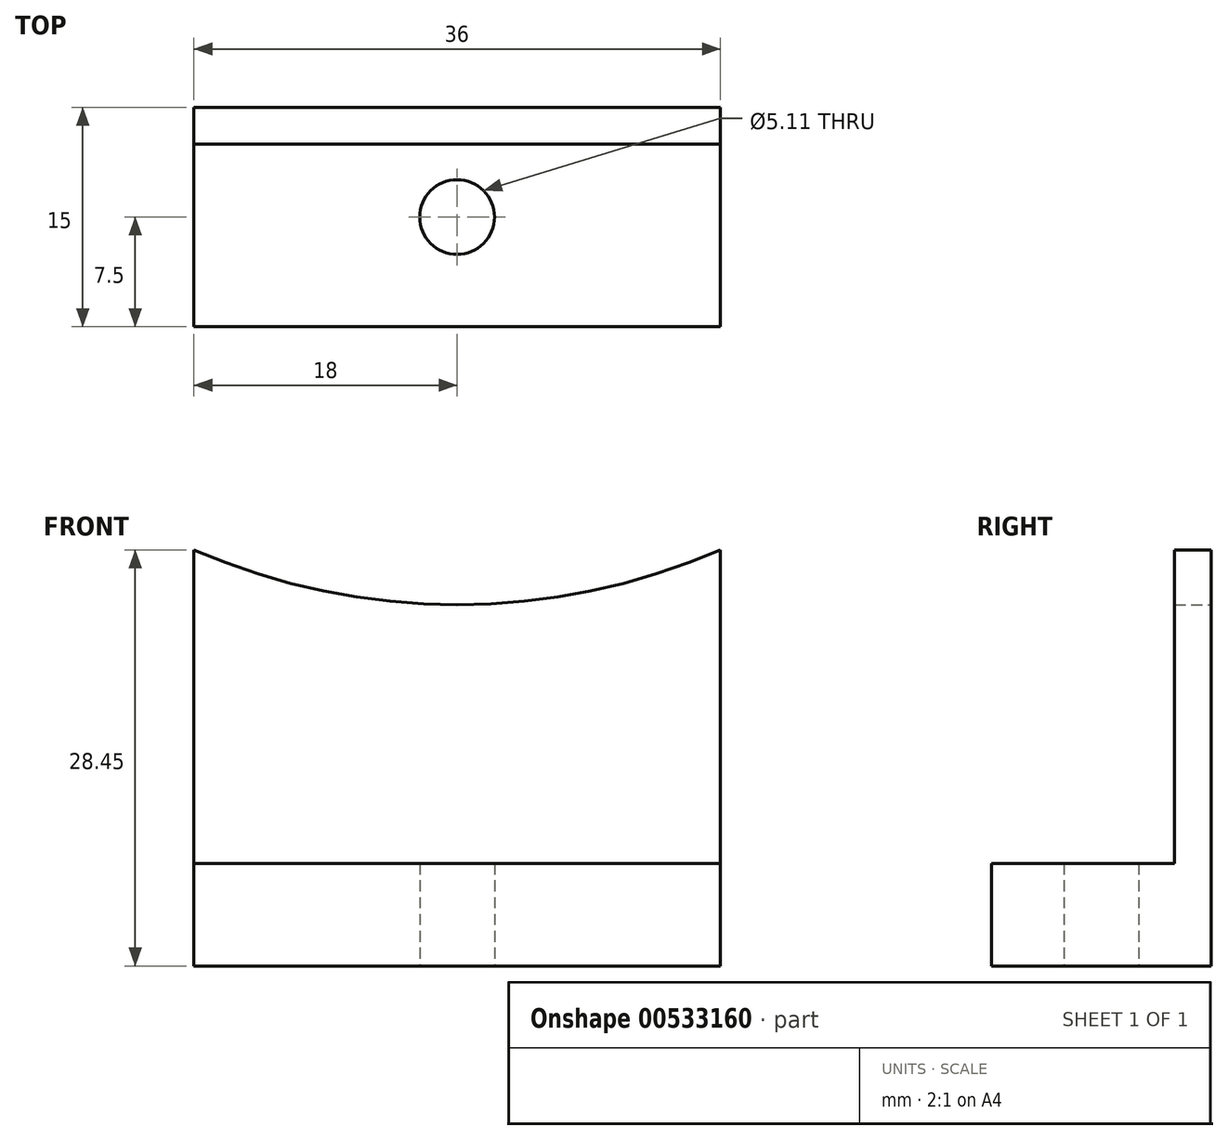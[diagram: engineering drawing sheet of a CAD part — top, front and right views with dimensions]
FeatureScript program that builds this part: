
annotation { "Feature Type Name" : "Feature", "Feature Type Description" : "" }
export const myFeature = defineFeature(function(context is Context, id is Id, definition is map)
    precondition{}
    {
        {
            var Q0;
            Q0=qCreatedBy(makeId("Top.planeOp"),FACE);
            var sketch = newSketch(context, id + "F0", { "sketchPlane" : qUnion([Q0])});
            skLineSegment(sketch, "E0.bottom", {"start": v(18, -7.5) * mm, "end": v(-18, -7.5) * mm});
            skLineSegment(sketch, "E0.top", {"start": v(18, 7.5) * mm, "end": v(-18, 7.5) * mm});
            skLineSegment(sketch, "E0.left", {"start": v(18, -7.5) * mm, "end": v(18, 7.5) * mm});
            skLineSegment(sketch, "E0.right", {"start": v(-18, -7.5) * mm, "end": v(-18, 7.5) * mm});
            skPoint(sketch, "E0.middle", {"position": v(0, 0) * mm});
            skSolve(sketch);
        }
        {
            var Q0;
            Q0 = qSketchRegion(id + "F0", true);
            extrude(context, id + "F1", {"entities" : qUnion([Q0]), "depth" : 7 * mm, "offsetDistance" : 25.4 * mm});
        }
        {
            var Q0;
            Q0=makeQuery(id+"F1.opExtrude","CAP_FACE",FACE,{"disambiguationData":[OSD([sQuery(id+"F0.wireOp",EDGE,"E0.bottom"),sQuery(id+"F0.wireOp",EDGE,"E0.top"),sQuery(id+"F0.wireOp",EDGE,"E0.left"),sQuery(id+"F0.wireOp",EDGE,"E0.right")])],"isStart":false});
            var sketch = newSketch(context, id + "F2", { "sketchPlane" : qUnion([Q0])});
            skLineSegment(sketch, "E1.bottom", {"start": v(-18, 7.5) * mm, "end": v(18, 7.5) * mm});
            skLineSegment(sketch, "E1.top", {"start": v(-18, 5) * mm, "end": v(18, 5) * mm});
            skLineSegment(sketch, "E1.left", {"start": v(-18, 7.5) * mm, "end": v(-18, 5) * mm});
            skLineSegment(sketch, "E1.right", {"start": v(18, 7.5) * mm, "end": v(18, 5) * mm});
            skSolve(sketch);
        }
        {
            var Q0;
            Q0 = qSketchRegion(id + "F2", true);
            extrude(context, id + "F3", {"entities" : qUnion([Q0]), "operationType" : NewBodyOperationType.ADD, "depth" : 30 * mm, "offsetDistance" : 25 * mm});
        }
        {
            var Q0;
            Q0=makeQuery(id+"F3.boolean.opBoolean","MERGE",FACE,{"derivedFrom":[makeQuery(id+"F1.opExtrude","SWEPT_FACE",FACE,{"disambiguationData":[OSD([sQuery(id+"F0.wireOp",EDGE,"E0.top")])]}),makeQuery(id+"F3.opExtrude","SWEPT_FACE",FACE,{"disambiguationData":[OSD([sQuery(id+"F2.wireOp",EDGE,"E1.bottom")])]})]});
            var sketch = newSketch(context, id + "F4", { "sketchPlane" : qUnion([Q0])});
            skLineSegment(sketch, "E2", {"start": v(0, 37) * mm, "end": v(0, 69.8) * mm, "construction": true});
            skArc(sketch, "E3", {"start": v(0, 71.32) * mm, "mid": v(0.32, 72.6) * mm, "end": v(-0.57, 71.63) * mm});
            skArc(sketch, "E4", {"start": v(-18, 28.45) * mm, "mid": v(0, 24.7) * mm, "end": v(18, 28.45) * mm});
            skSolve(sketch);
        }
        {
            var Q0;
            Q0 = qSketchRegion(id + "F4", true);
            var Q1;
            {var subQ0=sQuery(id+"F4.wireOp",EDGE,"E4");Q1=makeQuery(id+"F4.imprint","IMPRINT",FACE,{"disambiguationData":[TD([[makeQuery(id+"F4.imprint","IMPRINT",EDGE,{"derivedFrom":subQ0}),1.0]])]});}
            var Q2;
            Q2=makeQuery(id+"F3.opExtrude","SWEPT_FACE",FACE,{"disambiguationData":[OSD([sQuery(id+"F2.wireOp",EDGE,"E1.top")])]});
            extrude(context, id + "F5", {"entities" : qUnion([Q0, Q1, Q2]), "operationType" : NewBodyOperationType.REMOVE, "oppositeDirection" : true, "depth" : 25 * mm, "offsetDistance" : 25 * mm});
        }
        {
            var Q0;
            Q0=sQuery(id+"F0.wireOp",VERTEX,"E0.middle");
            var Q1;
            Q1=makeQuery(id+"F1.opExtrude","SWEPT_BODY",BODY,{"disambiguationData":[OSD([sQuery(id+"F0.wireOp",EDGE,"E0.bottom"),sQuery(id+"F0.wireOp",EDGE,"E0.top"),sQuery(id+"F0.wireOp",EDGE,"E0.left"),sQuery(id+"F0.wireOp",EDGE,"E0.right")])]});
            hole(context, id + "F6", {"style" : HoleStyle.SIMPLE, "endStyle" : HoleEndStyle.THROUGH, "oppositeDirection" : true, "standardTappedOrClearance" : lookupTablePath({ "fit" : "Normal (ASME)", "standard" : "ANSI", "engagement" : "75%", "pitch" : "20 tpi", "size" : "1/4", "type" : "Tapped" }), "standardBlindInLast" : lookupTablePath({ "fit" : "Free", "standard" : "ANSI", "engagement" : "75%", "pitch" : "20 tpi", "size" : "1/4", "type" : "Tapped" }), "holeDiameter" : 5.1 * mm, "showTappedDepth" : true, "isTappedThrough" : true, "tappedDepth" : 12 * mm, "tapClearance" : 3, "locations" : qUnion([Q0]), "scope" : qUnion([Q1]), "majorDiameter" : 6.35 * mm});
        }
    });
